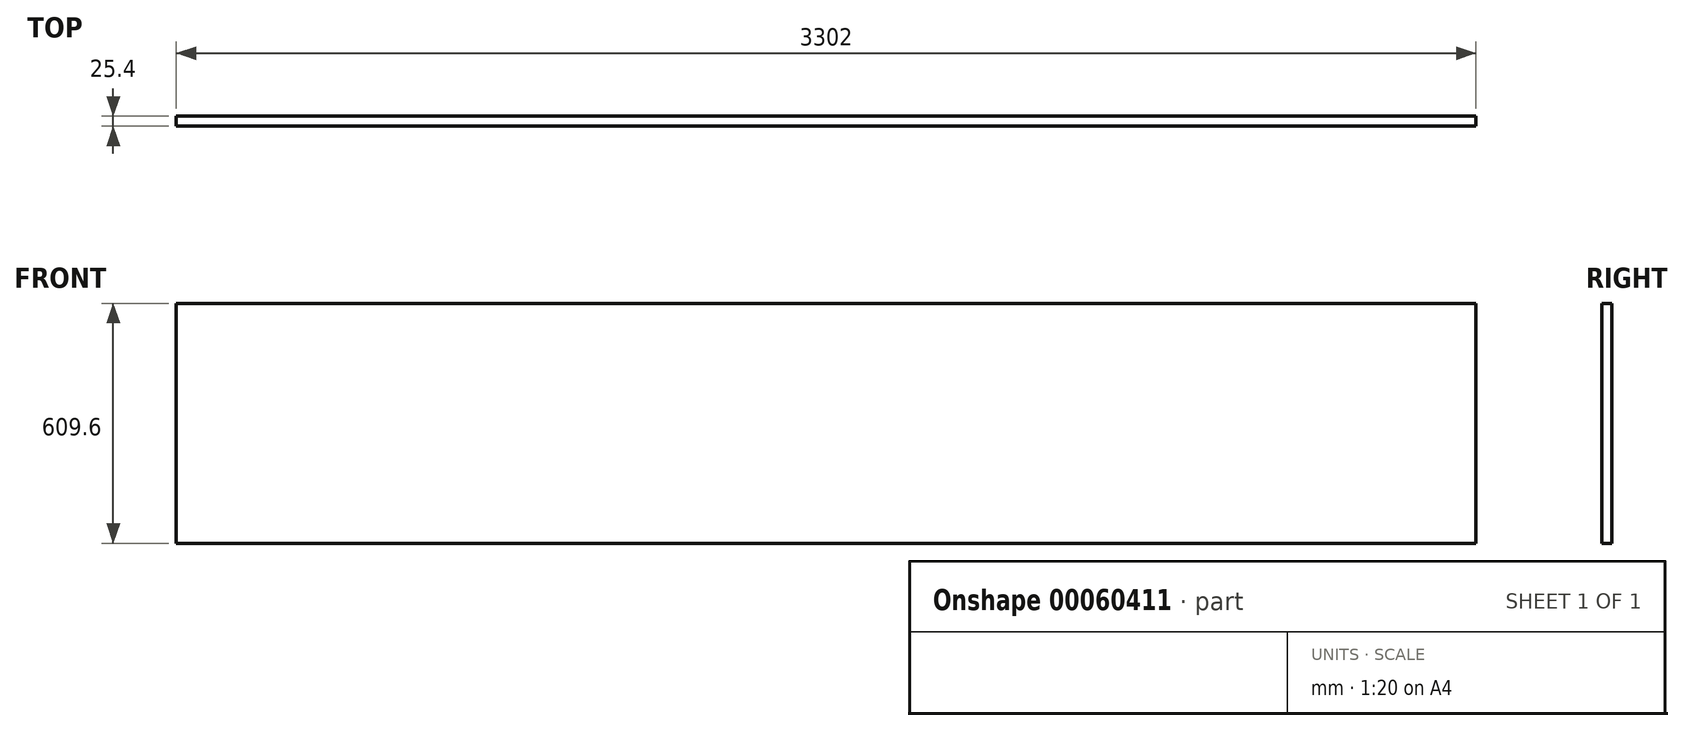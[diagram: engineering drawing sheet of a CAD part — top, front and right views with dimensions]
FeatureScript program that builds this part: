
annotation { "Feature Type Name" : "Feature", "Feature Type Description" : "" }
export const myFeature = defineFeature(function(context is Context, id is Id, definition is map)
    precondition{}
    {
        {
            var Q0;
            Q0=qCreatedBy(makeId("Right.planeOp"),FACE);
            var sketch = newSketch(context, id + "F0", { "sketchPlane" : qUnion([Q0])});
            skLineSegment(sketch, "E0.bottom", {"start": v(-25.4, 609.6) * mm, "end": v(0, 609.6) * mm});
            skLineSegment(sketch, "E0.top", {"start": v(-25.4, 0) * mm, "end": v(0, 0) * mm});
            skLineSegment(sketch, "E0.left", {"start": v(-25.4, 609.6) * mm, "end": v(-25.4, 0) * mm});
            skLineSegment(sketch, "E0.right", {"start": v(0, 609.6) * mm, "end": v(0, 0) * mm});
            skSolve(sketch);
        }
        {
            var Q0;
            Q0=makeQuery(id+"F0.imprint","IMPRINT",FACE,{"disambiguationData":[TD([[makeQuery(id+"F0.imprint","IMPRINT",EDGE,{"derivedFrom":sQuery(id+"F0.wireOp",EDGE,"E0.bottom")}),-1.0]])]});
            extrude(context, id + "F1", {"entities" : qUnion([Q0]), "depth" : 3302 * mm});
        }
    });
